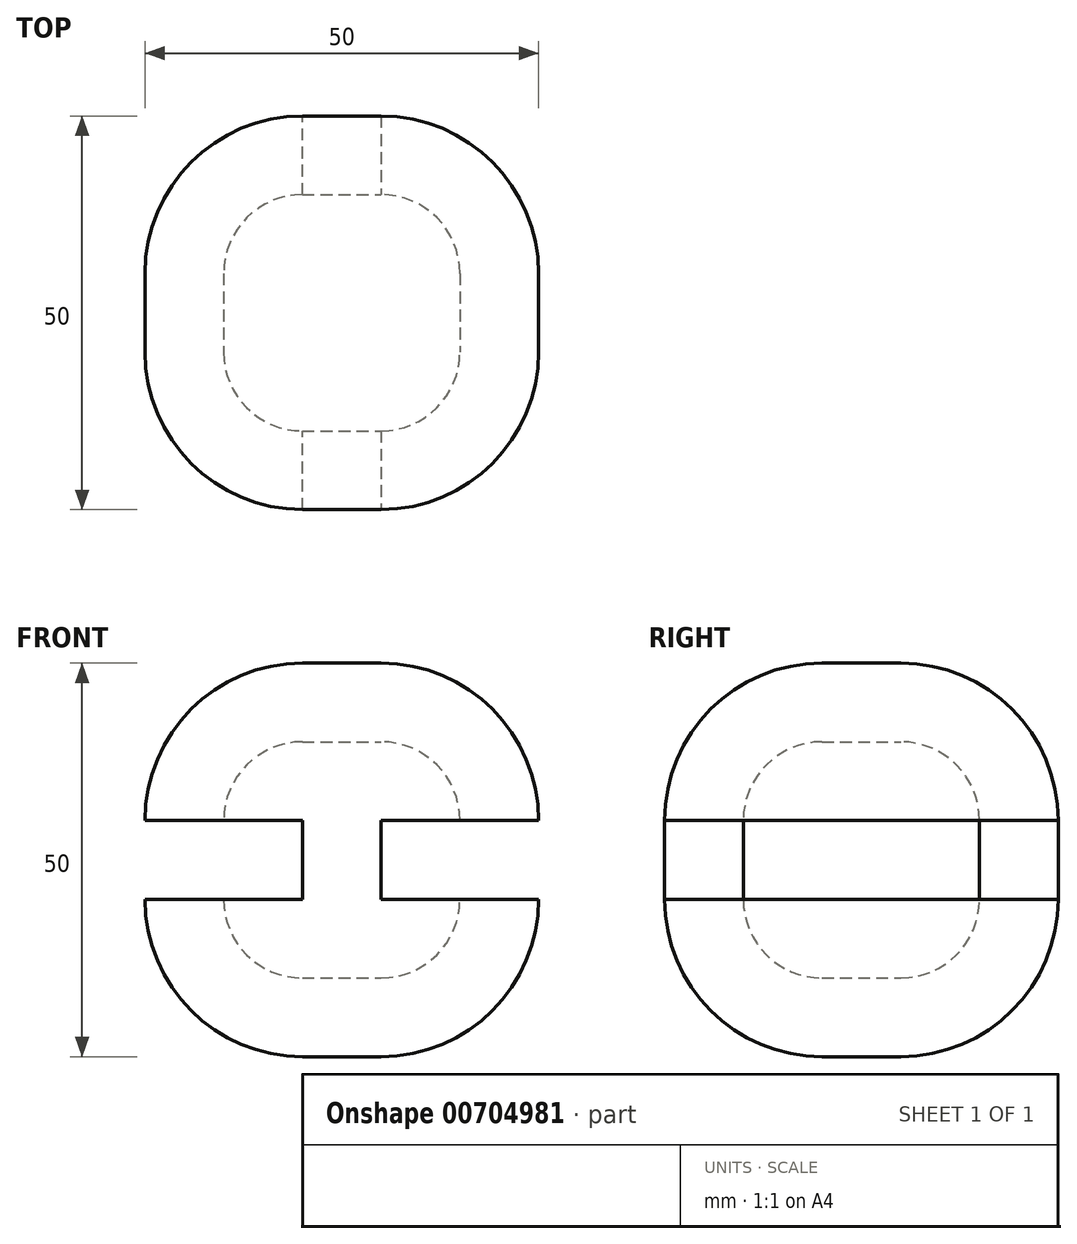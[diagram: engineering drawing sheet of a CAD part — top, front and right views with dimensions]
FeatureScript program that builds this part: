
annotation { "Feature Type Name" : "Feature", "Feature Type Description" : "" }
export const myFeature = defineFeature(function(context is Context, id is Id, definition is map)
    precondition{}
    {
        {
            var Q0;
            Q0=qCreatedBy(makeId("Top.planeOp"),FACE);
            var sketch = newSketch(context, id + "F0", { "sketchPlane" : qUnion([Q0])});
            skLineSegment(sketch, "E0.bottom", {"start": v(25, -25) * mm, "end": v(-25, -25) * mm});
            skLineSegment(sketch, "E0.top", {"start": v(25, 25) * mm, "end": v(-25, 25) * mm});
            skLineSegment(sketch, "E0.left", {"start": v(25, -25) * mm, "end": v(25, 25) * mm});
            skLineSegment(sketch, "E0.right", {"start": v(-25, -25) * mm, "end": v(-25, 25) * mm});
            skPoint(sketch, "E0.middle", {"position": v(0, 0) * mm});
            skSolve(sketch);
        }
        {
            var Q0;
            Q0 = qSketchRegion(id + "F0", true);
            extrude(context, id + "F1", {"entities" : qUnion([Q0]), "depth" : 50 * mm, "offsetDistance" : 25.4 * mm});
        }
        {
            var Q0;
            Q0=makeQuery(id+"F1.opExtrude","SWEPT_FACE",FACE,{"disambiguationData":[OSD([sQuery(id+"F0.wireOp",EDGE,"E0.bottom")])]});
            var Q1;
            Q1=makeQuery(id+"F1.opExtrude","SWEPT_FACE",FACE,{"disambiguationData":[OSD([sQuery(id+"F0.wireOp",EDGE,"E0.left")])]});
            var Q2;
            Q2=makeQuery(id+"F1.opExtrude","CAP_FACE",FACE,{"disambiguationData":[OSD([sQuery(id+"F0.wireOp",EDGE,"E0.bottom"),sQuery(id+"F0.wireOp",EDGE,"E0.top"),sQuery(id+"F0.wireOp",EDGE,"E0.left"),sQuery(id+"F0.wireOp",EDGE,"E0.right")])],"isStart":false});
            var Q3;
            Q3=makeQuery(id+"F1.opExtrude","CAP_FACE",FACE,{"disambiguationData":[OSD([sQuery(id+"F0.wireOp",EDGE,"E0.bottom"),sQuery(id+"F0.wireOp",EDGE,"E0.top"),sQuery(id+"F0.wireOp",EDGE,"E0.left"),sQuery(id+"F0.wireOp",EDGE,"E0.right")])],"isStart":true});
            var Q4;
            Q4=makeQuery(id+"F1.opExtrude","SWEPT_FACE",FACE,{"disambiguationData":[OSD([sQuery(id+"F0.wireOp",EDGE,"E0.top")])]});
            fillet(context, id + "F2", {"entities" : qUnion([Q0, Q1, Q2, Q3, Q4]), "radius" : 20 * mm, "tangentPropagation" : true, "allowEdgeOverflow" : false});
        }
        {
            var Q0;
            Q0=makeQuery(id+"F1.opExtrude","SWEPT_FACE",FACE,{"disambiguationData":[OSD([sQuery(id+"F0.wireOp",EDGE,"E0.left")])]});
            var Q1;
            {var subQ0=sQuery(id+"F0.wireOp",EDGE,"E0.left");var subQ1=sQuery(id+"F0.wireOp",EDGE,"E0.top");Q1=makeQuery(id+"F2.opFillet","BLEND_FACE",FACE,{"disambiguationData":[OSD([subQ1,subQ0]),TDD([makeQuery(id+"F1.opExtrude","SWEPT_EDGE",EDGE,{"disambiguationData":[OSD([subQ1,subQ0])]})])]});}
            var Q2;
            {var subQ0=sQuery(id+"F0.wireOp",EDGE,"E0.left");var subQ1=sQuery(id+"F0.wireOp",EDGE,"E0.bottom");Q2=makeQuery(id+"F2.opFillet","BLEND_FACE",FACE,{"disambiguationData":[OSD([subQ1,subQ0]),TDD([makeQuery(id+"F1.opExtrude","SWEPT_EDGE",EDGE,{"disambiguationData":[OSD([subQ1,subQ0])]})])]});}
            var Q3;
            {var subQ0=sQuery(id+"F0.wireOp",EDGE,"E0.right");var subQ1=sQuery(id+"F0.wireOp",EDGE,"E0.bottom");Q3=makeQuery(id+"F2.opFillet","BLEND_FACE",FACE,{"disambiguationData":[OSD([subQ1,subQ0]),TDD([makeQuery(id+"F1.opExtrude","SWEPT_EDGE",EDGE,{"disambiguationData":[OSD([subQ1,subQ0])]})])]});}
            var Q4;
            Q4=makeQuery(id+"F1.opExtrude","SWEPT_FACE",FACE,{"disambiguationData":[OSD([sQuery(id+"F0.wireOp",EDGE,"E0.right")])]});
            var Q5;
            {var subQ0=sQuery(id+"F0.wireOp",EDGE,"E0.right");var subQ1=sQuery(id+"F0.wireOp",EDGE,"E0.top");Q5=makeQuery(id+"F2.opFillet","BLEND_FACE",FACE,{"disambiguationData":[OSD([subQ1,subQ0]),TDD([makeQuery(id+"F1.opExtrude","SWEPT_EDGE",EDGE,{"disambiguationData":[OSD([subQ1,subQ0])]})])]});}
            var Q6;
            Q6=makeQuery(id+"F1.opExtrude","SWEPT_BODY",BODY,{"disambiguationData":[OSD([sQuery(id+"F0.wireOp",EDGE,"E0.bottom"),sQuery(id+"F0.wireOp",EDGE,"E0.top"),sQuery(id+"F0.wireOp",EDGE,"E0.left"),sQuery(id+"F0.wireOp",EDGE,"E0.right")])]});
            shell(context, id + "F3", {"entities" : qUnion([Q0, Q1, Q2, Q3, Q4, Q5]), "parts" : qUnion([Q6]), "thickness" : 10 * mm});
        }
    });
